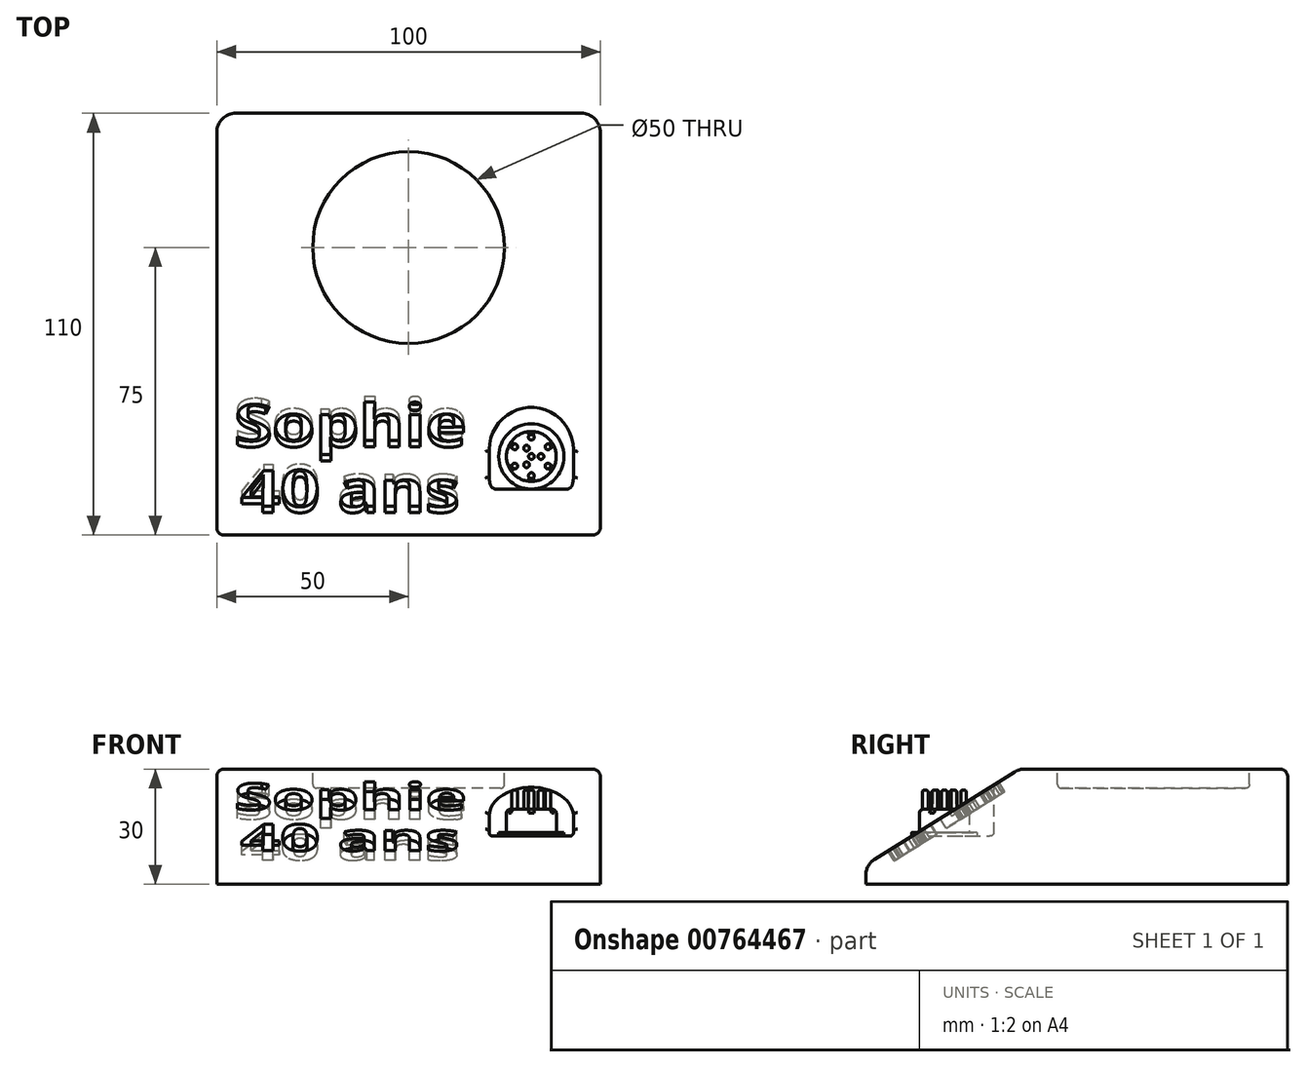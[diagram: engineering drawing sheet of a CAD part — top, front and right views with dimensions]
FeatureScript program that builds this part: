
annotation { "Feature Type Name" : "Feature", "Feature Type Description" : "" }
export const myFeature = defineFeature(function(context is Context, id is Id, definition is map)
    precondition{}
    {
        {
            var Q0;
            Q0=qCreatedBy(makeId("Right.planeOp"),FACE);
            var sketch = newSketch(context, id + "F0", { "sketchPlane" : qUnion([Q0])});
            skLineSegment(sketch, "E0", {"start": v(0, 0) * mm, "end": v(110, 0) * mm});
            skLineSegment(sketch, "E1", {"start": v(110, 0) * mm, "end": v(110, 30) * mm});
            skLineSegment(sketch, "E2", {"start": v(110, 30) * mm, "end": v(40, 30) * mm});
            skLineSegment(sketch, "E3", {"start": v(40, 30) * mm, "end": v(0, 5) * mm});
            skLineSegment(sketch, "E4", {"start": v(0, 5) * mm, "end": v(0, 0) * mm});
            skSolve(sketch);
        }
        {
            var Q0;
            Q0 = qSketchRegion(id + "F0", true);
            extrude(context, id + "F1", {"entities" : qUnion([Q0]), "depth" : 100 * mm, "offsetDistance" : 25 * mm});
        }
        {
            var Q0;
            Q0=makeQuery(id+"F1.opExtrude","SWEPT_FACE",FACE,{"disambiguationData":[OSD([sQuery(id+"F0.wireOp",EDGE,"E2")])]});
            var sketch = newSketch(context, id + "F2", { "sketchPlane" : qUnion([Q0])});
            skCircle(sketch, "E5", {"center": v(50, 75) * mm, "radius": 25 * mm});
            skPoint(sketch, "E5.centerSnap0", {"position": v(50, 110) * mm});
            skPoint(sketch, "E5.centerSnap1", {"position": v(0, 75) * mm});
            skSolve(sketch);
        }
        {
            var Q0;
            Q0 = qSketchRegion(id + "F2", true);
            extrude(context, id + "F3", {"entities" : qUnion([Q0]), "operationType" : NewBodyOperationType.REMOVE, "oppositeDirection" : true, "depth" : 5 * mm, "offsetDistance" : 25 * mm});
        }
        {
            var Q0;
            Q0=makeQuery(id+"F1.opExtrude","SWEPT_FACE",FACE,{"disambiguationData":[OSD([sQuery(id+"F0.wireOp",EDGE,"E3")])]});
            var sketch = newSketch(context, id + "F4", { "sketchPlane" : qUnion([Q0])});
            skText(sketch, "E6", { "text": "Sophie", "fontName": "OpenSans-Bold.ttf"});
            skText(sketch, "E7", { "text": "40 ans", "fontName": "OpenSans-Bold.ttf"});
            const initialGuessF4  = {"E6": [0.0045, 0.02982, 1, 0, 0.013], "E7": [0.00623, 0.00965, 1, 0, 0.013]};
            skSetInitialGuess(sketch, initialGuessF4);
            skSolve(sketch);
        }
        {
            var Q0;
            Q0 = qSketchRegion(id + "F4", true);
            extrude(context, id + "F5", {"entities" : qUnion([Q0]), "operationType" : NewBodyOperationType.REMOVE, "oppositeDirection" : true, "depth" : 3 * mm, "offsetDistance" : 25 * mm});
        }
        {
            var Q0;
            Q0=makeQuery(id+"F1.opExtrude","CAP_EDGE",EDGE,{"disambiguationData":[OSD([sQuery(id+"F0.wireOp",EDGE,"E1")])],"isStart":false});
            var Q1;
            Q1=makeQuery(id+"F1.opExtrude","CAP_EDGE",EDGE,{"disambiguationData":[OSD([sQuery(id+"F0.wireOp",EDGE,"E1")])],"isStart":true});
            var Q2;
            Q2=makeQuery(id+"F1.opExtrude","SWEPT_EDGE",EDGE,{"disambiguationData":[OSD([sQuery(id+"F0.wireOp",EDGE,"E2"),sQuery(id+"F0.wireOp",EDGE,"E3")])]});
            var Q3;
            Q3=makeQuery(id+"F1.opExtrude","SWEPT_EDGE",EDGE,{"disambiguationData":[OSD([sQuery(id+"F0.wireOp",EDGE,"E3"),sQuery(id+"F0.wireOp",EDGE,"E4")])]});
            fillet(context, id + "F6", {"entities" : qUnion([Q0, Q1, Q2, Q3]), "radius" : 5 * mm, "tangentPropagation" : true, "allowEdgeOverflow" : false});
        }
        {
            var Q0;
            Q0=makeQuery(id+"F1.opExtrude","CAP_EDGE",EDGE,{"disambiguationData":[OSD([sQuery(id+"F0.wireOp",EDGE,"E2")])],"isStart":true});
            fillet(context, id + "F7", {"entities" : qUnion([Q0]), "radius" : 2 * mm, "tangentPropagation" : true, "allowEdgeOverflow" : false});
        }
        {
            var Q0;
            Q0=makeQuery(id+"F3.boolean.opBoolean","COPY",EDGE,{"derivedFrom":makeQuery(id+"F3.opExtrude","CAP_EDGE",EDGE,{"disambiguationData":[OSD([sQuery(id+"F2.wireOp",EDGE,"E5")])],"isStart":false})});
            var Q1;
            Q1=makeQuery(id+"F3.boolean.opBoolean","COPY",EDGE,{"derivedFrom":makeQuery(id+"F3.opExtrude","CAP_EDGE",EDGE,{"disambiguationData":[OSD([sQuery(id+"F2.wireOp",EDGE,"E5")])],"isStart":true})});
            fillet(context, id + "F8", {"entities" : qUnion([Q0, Q1]), "radius" : 1 * mm, "tangentPropagation" : true, "allowEdgeOverflow" : false});
        }
        {
            var Q0;
            Q0=qCreatedBy(makeId("Top.planeOp"),FACE);
            cPlane(context, id + "F9", {"entities" : qUnion([Q0]), "cplaneType" : CPlaneType.OFFSET, "offset" : 12.5 * mm, "width" : 150 * mm, "height" : 150 * mm});
        }
        {
            var Q0;
            Q0=qCreatedBy(id+"F9.planeOp",FACE);
            var sketch = newSketch(context, id + "F10", { "sketchPlane" : qUnion([Q0])});
            skLineSegment(sketch, "E8.0", {"start": v(2, 2.35) * mm, "end": v(98, 2.35) * mm});
            skLineSegment(sketch, "E9.bottom", {"start": v(71, 2.35) * mm, "end": v(93, 2.35) * mm});
            skLineSegment(sketch, "E9.top", {"start": v(71, 22.35) * mm, "end": v(93, 22.35) * mm});
            skLineSegment(sketch, "E9.left", {"start": v(71, 2.35) * mm, "end": v(71, 22.35) * mm});
            skLineSegment(sketch, "E9.right", {"start": v(93, 2.35) * mm, "end": v(93, 22.35) * mm});
            skArc(sketch, "E10", {"start": v(93, 22.35) * mm, "mid": v(82, 33.35) * mm, "end": v(71, 22.35) * mm});
            skSolve(sketch);
        }
        {
            var Q0;
            Q0 = qSketchRegion(id + "F10", true);
            extrude(context, id + "F11", {"entities" : qUnion([Q0]), "operationType" : NewBodyOperationType.REMOVE, "depth" : 25 * mm, "offsetDistance" : 25 * mm});
        }
        {
            var Q0;
            Q0=makeQuery(id+"F11.boolean.opBoolean","COPY",FACE,{"derivedFrom":makeQuery(id+"F11.opExtrude","CAP_FACE",FACE,{"disambiguationData":[OSD([sQuery(id+"F10.wireOp",EDGE,"E9.bottom"),sQuery(id+"F10.wireOp",EDGE,"E9.left"),sQuery(id+"F10.wireOp",EDGE,"E9.right"),sQuery(id+"F10.wireOp",EDGE,"E10")])],"isStart":true})});
            var sketch = newSketch(context, id + "F12", { "sketchPlane" : qUnion([Q0])});
            skCircle(sketch, "E11", {"center": v(82, 20.5) * mm, "radius": 8.5 * mm});
            skPoint(sketch, "E11.centerSnap0", {"position": v(82, 5.5) * mm});
            skSolve(sketch);
        }
        {
            var Q0;
            Q0 = qSketchRegion(id + "F12", true);
            extrude(context, id + "F13", {"entities" : qUnion([Q0]), "operationType" : NewBodyOperationType.ADD, "depth" : 1 * mm, "offsetDistance" : 25 * mm});
        }
        {
            var Q0;
            Q0=makeQuery(id+"F13.opExtrude","CAP_FACE",FACE,{"disambiguationData":[OSD([sQuery(id+"F12.wireOp",EDGE,"E11")])],"isStart":false});
            var sketch = newSketch(context, id + "F14", { "sketchPlane" : qUnion([Q0])});
            skCircle(sketch, "E12", {"center": v(82, 20.5) * mm, "radius": 6.5 * mm});
            skSolve(sketch);
        }
        {
            var Q0;
            Q0 = qSketchRegion(id + "F14", true);
            extrude(context, id + "F15", {"entities" : qUnion([Q0]), "operationType" : NewBodyOperationType.ADD, "depth" : 6 * mm, "offsetDistance" : 25 * mm});
        }
        {
            var Q0;
            Q0=makeQuery(id+"F15.opExtrude","CAP_FACE",FACE,{"disambiguationData":[OSD([sQuery(id+"F14.wireOp",EDGE,"E12")])],"isStart":false});
            var sketch = newSketch(context, id + "F16", { "sketchPlane" : qUnion([Q0])});
            skCircle(sketch, "E13", {"center": v(82, 20.5) * mm, "radius": 0.75 * mm});
            skCircle(sketch, "E14", {"center": v(82, 25.5) * mm, "radius": 0.75 * mm});
            skCircle(sketch, "E15", {"center": v(84.5, 20.5) * mm, "radius": 0.75 * mm});
            skCircle(sketch, "E16.1.0", {"center": v(77.67, 23) * mm, "radius": 0.75 * mm});
            skCircle(sketch, "E16.2.0", {"center": v(77.67, 18) * mm, "radius": 0.75 * mm});
            skCircle(sketch, "E16.3.0", {"center": v(82, 15.5) * mm, "radius": 0.75 * mm});
            skCircle(sketch, "E16.4.0", {"center": v(86.33, 18) * mm, "radius": 0.75 * mm});
            skCircle(sketch, "E16.5.0", {"center": v(86.33, 23) * mm, "radius": 0.75 * mm});
            skCircle(sketch, "E17.1.0", {"center": v(80.75, 22.67) * mm, "radius": 0.75 * mm});
            skCircle(sketch, "E17.2.0", {"center": v(80.75, 18.33) * mm, "radius": 0.75 * mm});
            skSolve(sketch);
        }
        {
            var Q0;
            Q0 = qSketchRegion(id + "F16", true);
            extrude(context, id + "F17", {"entities" : qUnion([Q0]), "operationType" : NewBodyOperationType.ADD, "depth" : 5 * mm, "offsetDistance" : 25 * mm});
        }
        {
            var Q0;
            {var subQ1=sQuery(id+"F0.wireOp",EDGE,"E2");var subQ2=sQuery(id+"F0.wireOp",EDGE,"E3");Q0=makeQuery(id+"F11.boolean.opBoolean","INTERSECT",EDGE,{"derivedFrom":[makeQuery(id+"F5.boolean.opBoolean","SPLIT",FACE,{"disambiguationData":[TD([makeQuery(id+"F1.opExtrude","SWEPT_FACE",FACE,{"disambiguationData":[OSD([subQ1])]})])],"derivedFrom":makeQuery(id+"F1.opExtrude","SWEPT_FACE",FACE,{"disambiguationData":[OSD([subQ2])]})}),makeQuery(id+"F11.opExtrude","SWEPT_FACE",FACE,{"disambiguationData":[OSD([sQuery(id+"F10.wireOp",EDGE,"E10")])]})]});}
            var Q1;
            Q1=makeQuery(id+"F11.boolean.opBoolean","COPY",EDGE,{"derivedFrom":makeQuery(id+"F11.opExtrude","CAP_EDGE",EDGE,{"disambiguationData":[OSD([sQuery(id+"F10.wireOp",EDGE,"E10")])],"isStart":true})});
            var Q2;
            Q2=makeQuery(id+"F15.opExtrude","CAP_EDGE",EDGE,{"disambiguationData":[OSD([sQuery(id+"F14.wireOp",EDGE,"E12")])],"isStart":false});
            fillet(context, id + "F18", {"entities" : qUnion([Q0, Q1, Q2]), "radius" : 1 * mm, "tangentPropagation" : true, "allowEdgeOverflow" : false});
        }
        {
            var Q0;
            Q0=makeQuery(id+"F17.opExtrude","CAP_FACE",FACE,{"disambiguationData":[OSD([sQuery(id+"F16.wireOp",EDGE,"E16.2.0")])],"isStart":false});
            var Q1;
            Q1=makeQuery(id+"F17.opExtrude","CAP_FACE",FACE,{"disambiguationData":[OSD([sQuery(id+"F16.wireOp",EDGE,"E16.1.0")])],"isStart":false});
            var Q2;
            Q2=makeQuery(id+"F17.opExtrude","CAP_FACE",FACE,{"disambiguationData":[OSD([sQuery(id+"F16.wireOp",EDGE,"E14")])],"isStart":false});
            var Q3;
            Q3=makeQuery(id+"F17.opExtrude","CAP_FACE",FACE,{"disambiguationData":[OSD([sQuery(id+"F16.wireOp",EDGE,"E17.1.0")])],"isStart":false});
            var Q4;
            Q4=makeQuery(id+"F17.opExtrude","CAP_FACE",FACE,{"disambiguationData":[OSD([sQuery(id+"F16.wireOp",EDGE,"E13")])],"isStart":false});
            var Q5;
            Q5=makeQuery(id+"F17.opExtrude","CAP_FACE",FACE,{"disambiguationData":[OSD([sQuery(id+"F16.wireOp",EDGE,"E17.2.0")])],"isStart":false});
            var Q6;
            Q6=makeQuery(id+"F17.opExtrude","CAP_FACE",FACE,{"disambiguationData":[OSD([sQuery(id+"F16.wireOp",EDGE,"E16.3.0")])],"isStart":false});
            var Q7;
            Q7=makeQuery(id+"F17.opExtrude","CAP_FACE",FACE,{"disambiguationData":[OSD([sQuery(id+"F16.wireOp",EDGE,"E15")])],"isStart":false});
            var Q8;
            Q8=makeQuery(id+"F17.opExtrude","CAP_FACE",FACE,{"disambiguationData":[OSD([sQuery(id+"F16.wireOp",EDGE,"E16.5.0")])],"isStart":false});
            var Q9;
            Q9=makeQuery(id+"F17.opExtrude","CAP_FACE",FACE,{"disambiguationData":[OSD([sQuery(id+"F16.wireOp",EDGE,"E16.4.0")])],"isStart":false});
            fillet(context, id + "F19", {"entities" : qUnion([Q0, Q1, Q2, Q3, Q4, Q5, Q6, Q7, Q8, Q9]), "radius" : 0.5 * mm, "tangentPropagation" : true, "allowEdgeOverflow" : false});
        }
    });
